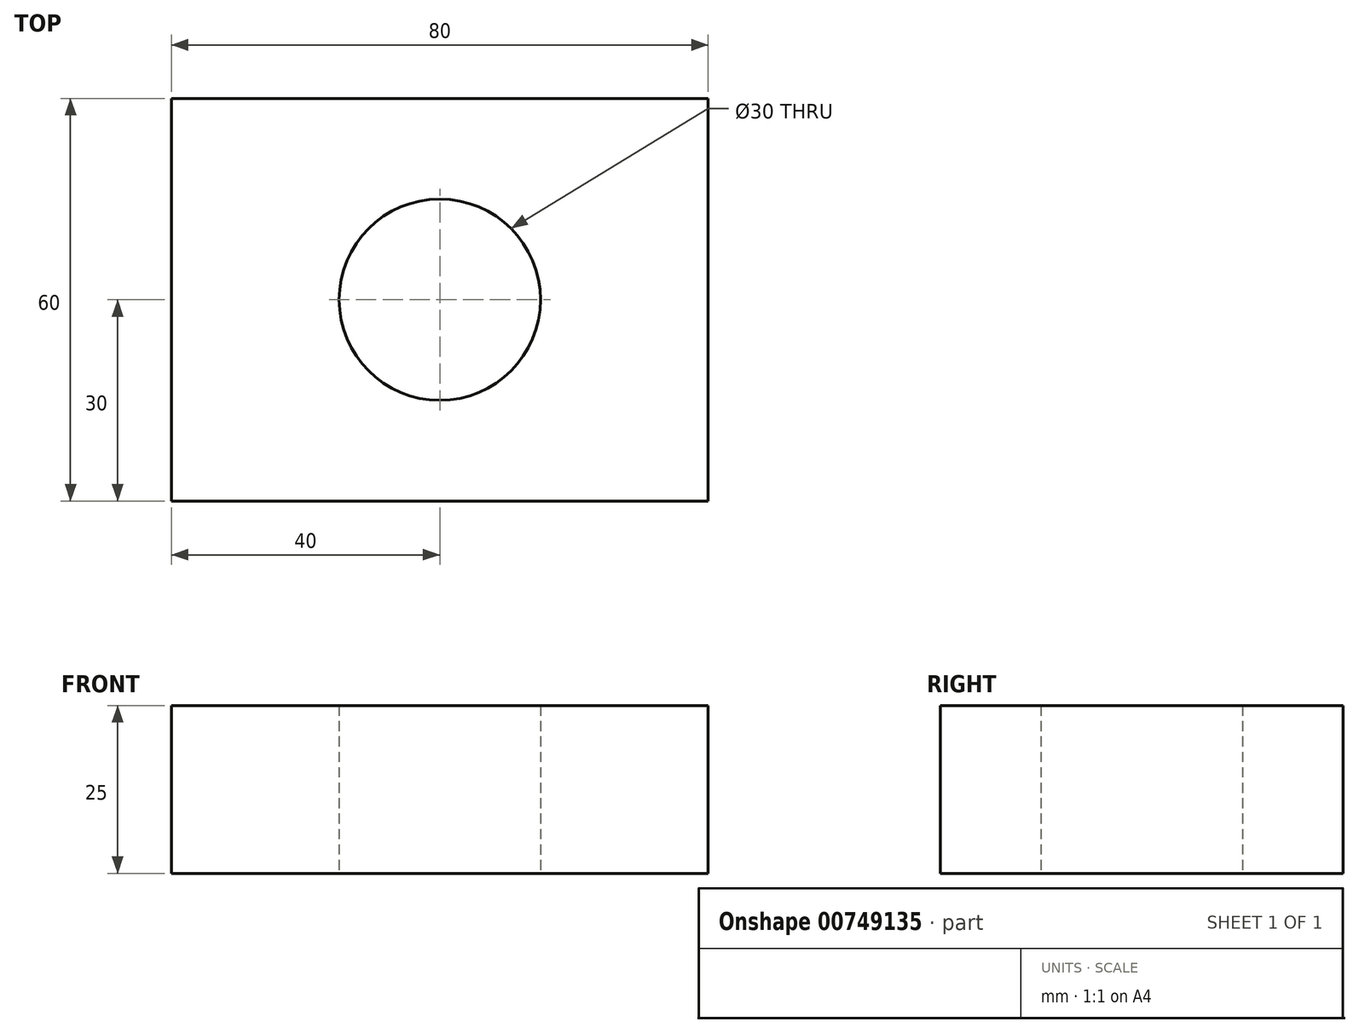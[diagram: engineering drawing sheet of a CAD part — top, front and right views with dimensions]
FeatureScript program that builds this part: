
annotation { "Feature Type Name" : "Feature", "Feature Type Description" : "" }
export const myFeature = defineFeature(function(context is Context, id is Id, definition is map)
    precondition{}
    {
        {
            var Q0;
            Q0=qCreatedBy(makeId("Top.planeOp"),FACE);
            var sketch = newSketch(context, id + "F0", { "sketchPlane" : qUnion([Q0])});
            skLineSegment(sketch, "E0.bottom", {"start": v(-40, 30) * mm, "end": v(40, 30) * mm});
            skLineSegment(sketch, "E0.top", {"start": v(-40, -30) * mm, "end": v(40, -30) * mm});
            skLineSegment(sketch, "E0.left", {"start": v(-40, 30) * mm, "end": v(-40, -30) * mm});
            skLineSegment(sketch, "E0.right", {"start": v(40, 30) * mm, "end": v(40, -30) * mm});
            skCircle(sketch, "E1", {"center": v(0, 0) * mm, "radius": 15 * mm});
            skSolve(sketch);
        }
        {
            var Q0;
            Q0 = qSketchRegion(id + "F0", true);
            extrude(context, id + "F1", {"entities" : qUnion([Q0]), "depth" : 25 * mm, "offsetDistance" : 25 * mm});
        }
    });
